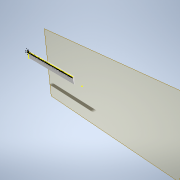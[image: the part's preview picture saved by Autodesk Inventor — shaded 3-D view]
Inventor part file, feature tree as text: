
AUTODESK INVENTOR PART (.ipt)
format: ipt  version: 2021 (Build 250183000, 183)  size: 430,080 bytes
history: native  units: mm
features: sketch x3, other x2, extrude x2, chamfer x1, pattern_linear x1
ambient origin geometry x8: Origin, YZ Plane, XZ Plane, XY Plane, X Axis, Y Axis, Z Axis, Center Point
bodies: Body1 (feature_tree), Body2 (feature_tree)
feature tree (9):
  other  "Bryła1"
  other  "Płaszczyzna konstrukcyjna1"
  extrude  "Wyciągnięcie proste1"  Depth=400.0mm
  chamfer  "Faza1"  Distance=50.0mm
  sketch  "Szkic2"
  extrude  "Wyciągnięcie proste2"  Depth=10.0mm TaperAngle=0.0deg
  pattern_linear  "Szyk prostokątny1"  Spacing1=34.0mm  [1 undecoded]
  sketch  "Szkic1"
  sketch  "Szkic3"
note: 1 required parameter value undecoded (feature->parameter linkage not recoverable at this tier; creation-order binding heuristic only, values carry confidence <= 0.55)
